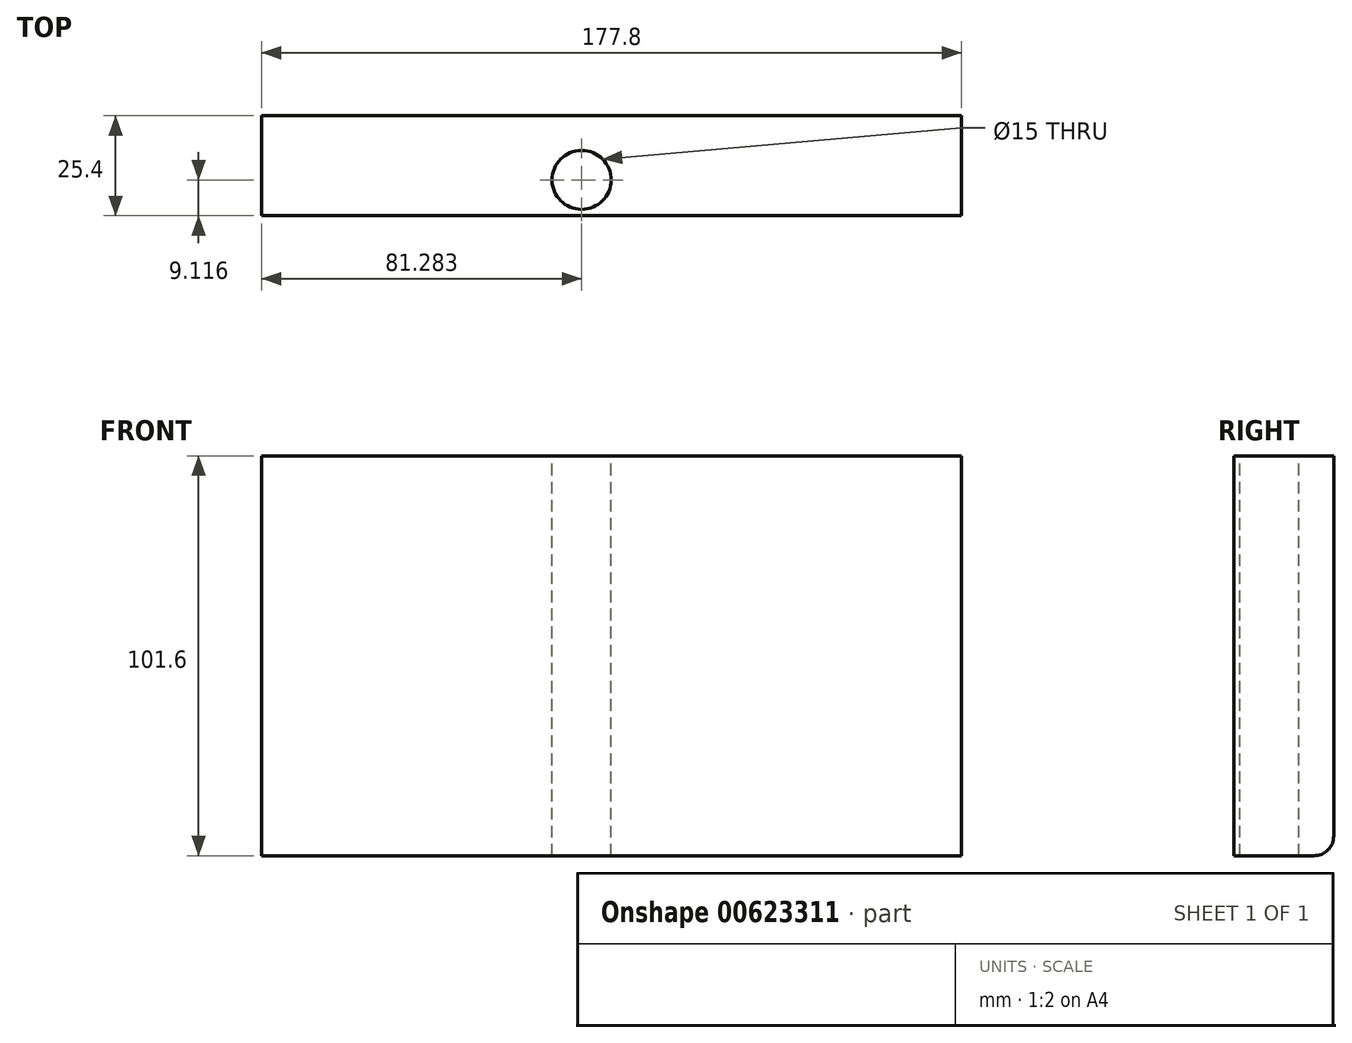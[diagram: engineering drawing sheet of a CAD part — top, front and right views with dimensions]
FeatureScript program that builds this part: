
annotation { "Feature Type Name" : "Feature", "Feature Type Description" : "" }
export const myFeature = defineFeature(function(context is Context, id is Id, definition is map)
    precondition{}
    {
        {
            var Q0;
            Q0=qCreatedBy(makeId("Front.planeOp"),FACE);
            var sketch = newSketch(context, id + "F0", { "sketchPlane" : qUnion([Q0])});
            skLineSegment(sketch, "E0.bottom", {"start": v(-140.55, 78.74) * mm, "end": v(37.25, 78.74) * mm});
            skLineSegment(sketch, "E0.top", {"start": v(-140.55, -22.86) * mm, "end": v(37.25, -22.86) * mm});
            skLineSegment(sketch, "E0.left", {"start": v(-140.55, 78.74) * mm, "end": v(-140.55, -22.86) * mm});
            skLineSegment(sketch, "E0.right", {"start": v(37.25, 78.74) * mm, "end": v(37.25, -22.86) * mm});
            skSolve(sketch);
        }
        {
            var Q0;
            Q0 = qSketchRegion(id + "F0", true);
            extrude(context, id + "F1", {"entities" : qUnion([Q0]), "depth" : 25.4 * mm, "offsetDistance" : 25.4 * mm});
        }
        {
            var Q0;
            Q0=makeQuery(id+"F1.opExtrude","SWEPT_FACE",FACE,{"disambiguationData":[OSD([sQuery(id+"F0.wireOp",EDGE,"E0.bottom")])]});
            var sketch = newSketch(context, id + "F2", { "sketchPlane" : qUnion([Q0])});
            skCircle(sketch, "E1", {"center": v(-59.27, -16.28) * mm, "radius": 7.5 * mm});
            skSolve(sketch);
        }
        {
            var Q0;
            Q0 = qSketchRegion(id + "F2", true);
            extrude(context, id + "F3", {"entities" : qUnion([Q0]), "operationType" : NewBodyOperationType.REMOVE, "oppositeDirection" : true, "depth" : 150 * mm, "offsetDistance" : 25 * mm});
        }
        {
            var Q0;
            Q0=makeQuery(id+"F1.opExtrude","CAP_EDGE",EDGE,{"disambiguationData":[OSD([sQuery(id+"F0.wireOp",EDGE,"E0.top")])],"isStart":true});
            fillet(context, id + "F4", {"entities" : qUnion([Q0]), "radius" : 5 * mm, "tangentPropagation" : true, "allowEdgeOverflow" : false});
        }
    });
